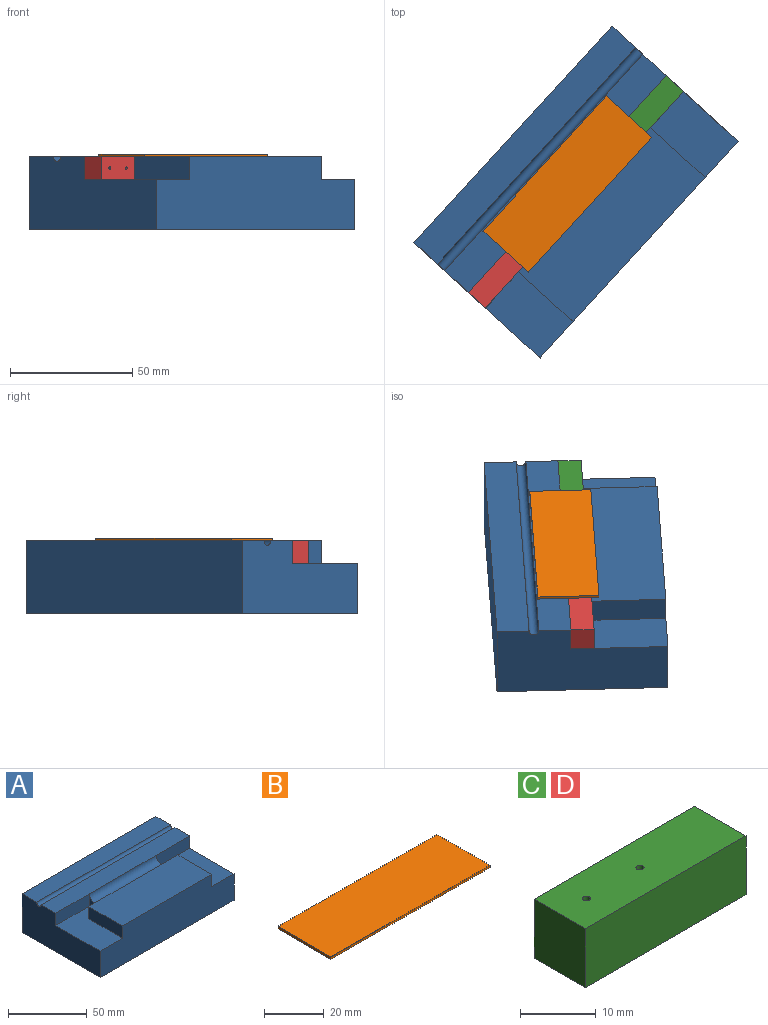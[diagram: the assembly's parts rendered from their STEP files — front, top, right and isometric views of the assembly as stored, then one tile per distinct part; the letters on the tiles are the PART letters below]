
ASSEMBLY  parts=4 mates=3
PART A: 20 faces, bbox 120x70x30 mm
  f0: plane 120x30mm, normal (0,-1,0), area 3219mm2, adj f1,f3,f4,f10,f11,f15,f18,f19
  f1: plane 70x30mm, normal (1,0,0), area 1715mm2, adj f0,f6,f8,f9,f10,f11,f12,f17
  f2: plane 10x9.53mm, normal (0,1,0), area 95.3mm2, adj f4,f11,f13,f19
  f3: plane 70x30mm, normal (-1,0,0), area 1715mm2, adj f0,f6,f8,f9,f10,f14,f15,f17
  f4: plane 80x30.24mm, normal (0,0,1), area 2419mm2, adj f0,f2,f5,f7,f18,f19
  f5: plane 10x9.53mm, normal (0,1,0), area 95.3mm2, adj f4,f15,f16,f18
  f6: plane 120x13.12mm, normal (0,0,1), area 1574.3mm2, adj f1,f3,f9,f17
  f7: cylinder r=4.76mm len=60mm, axis (1,0,0), area 897.7mm2, adj f4,f8,f13,f16
  f8: plane 120x13.12mm, normal (0,0,1), area 1574.2mm2, adj f1,f3,f7,f12,f14,f17
  f9: plane 120x30mm, normal (0,1,0), area 3600mm2, adj f1,f3,f6,f10
  f10: plane 120x70mm, normal (0,0,-1), area 8400mm2, adj f0,f1,f3,f9
  f11: plane 39.76x30mm, normal (0,0,1), area 890.5mm2, adj f0,f1,f2,f12,f13,f19
  f12: plane 30x9.53mm, normal (0,-1,0), area 285.7mm2, adj f1,f8,f11,f13
  f13: plane 9.53x9.53mm, normal (1,0,0), area 55.1mm2, adj f2,f7,f11,f12
  f14: plane 30x9.53mm, normal (0,-1,0), area 285.7mm2, adj f3,f8,f15,f16
  f15: plane 39.76x30mm, normal (0,0,1), area 890.5mm2, adj f0,f3,f5,f14,f16,f18
  f16: plane 9.53x9.53mm, normal (-1,0,0), area 55.1mm2, adj f5,f7,f14,f15
  f17: cylinder r=2mm len=120mm, axis (1,0,0), area 754mm2, adj f1,f3,f6,f8
  f18: plane 30.24x9.53mm, normal (-1,0,0), area 288mm2, adj f0,f4,f5,f15
  f19: plane 30.24x9.53mm, normal (1,0,0), area 288mm2, adj f0,f2,f4,f11
PART B: 6 faces, bbox 75x25x1 mm
  f0: plane 25x1mm, normal (1,0,0), area 25mm2, adj f1,f3,f4,f5
  f1: plane 75x1mm, normal (0,1,0), area 75mm2, adj f0,f2,f4,f5
  f2: plane 25x1mm, normal (-1,0,0), area 25mm2, adj f1,f3,f4,f5
  f3: plane 75x1mm, normal (0,-1,0), area 75mm2, adj f0,f2,f4,f5
  f4: plane 75x25mm, normal (0,0,1), area 1875mm2, adj f0,f1,f2,f3
  f5: plane 75x25mm, normal (0,0,-1), area 1875mm2, adj f0,f1,f2,f3
PART C: 8 faces, bbox 30x9.5x9.5 mm
  f0: plane 30x9.53mm, normal (0,1,0), area 285.7mm2, adj f1,f3,f4,f5
  f1: plane 30x9.53mm, normal (0,0,1), area 284mm2, adj f0,f2,f4,f5,f6,f7
  f2: plane 30x9.53mm, normal (0,-1,0), area 285.7mm2, adj f1,f3,f4,f5
  f3: plane 30x9.53mm, normal (0,0,-1), area 284mm2, adj f0,f2,f4,f5,f6,f7
  f4: plane 9.53x9.53mm, normal (1,0,0), area 90.7mm2, adj f0,f1,f2,f3
  f5: plane 9.53x9.53mm, normal (-1,0,0), area 90.7mm2, adj f0,f1,f2,f3
  f6: cylinder r=0.53mm len=9.53mm, axis (0,0,1), area 31.7mm2, adj f1,f3
  f7: cylinder r=0.53mm len=9.53mm, axis (0,0,1), area 31.7mm2, adj f1,f3
PART D: same geometry as C
PLACE A rot(axis=(0,0,1),47.5deg) t=(15.11,-54.13,-5.39)mm
PLACE B rot(axis=(0,0,1),47.5deg) t=(11.6,-50.91,24.61)mm
PLACE C rot(axis=(-0.3,0.68,-0.68),146.9deg) t=(55.62,-9.87,19.85)mm
PLACE D rot(axis=(0.85,0.37,0.37),99.3deg) t=(-25.39,-98.39,19.85)mm
MATE fastened D.f2 <-> A.f15  axis (0,0,-1) through (-28.91,-95.18,15.09)mm
MATE fastened C.f0 <-> A.f11  axis (0,0,-1) through (52.11,-6.65,15.09)mm
MATE fastened B.f5 <-> A.f8  axis (0,0,-1) through (11.6,-50.91,24.61)mm
